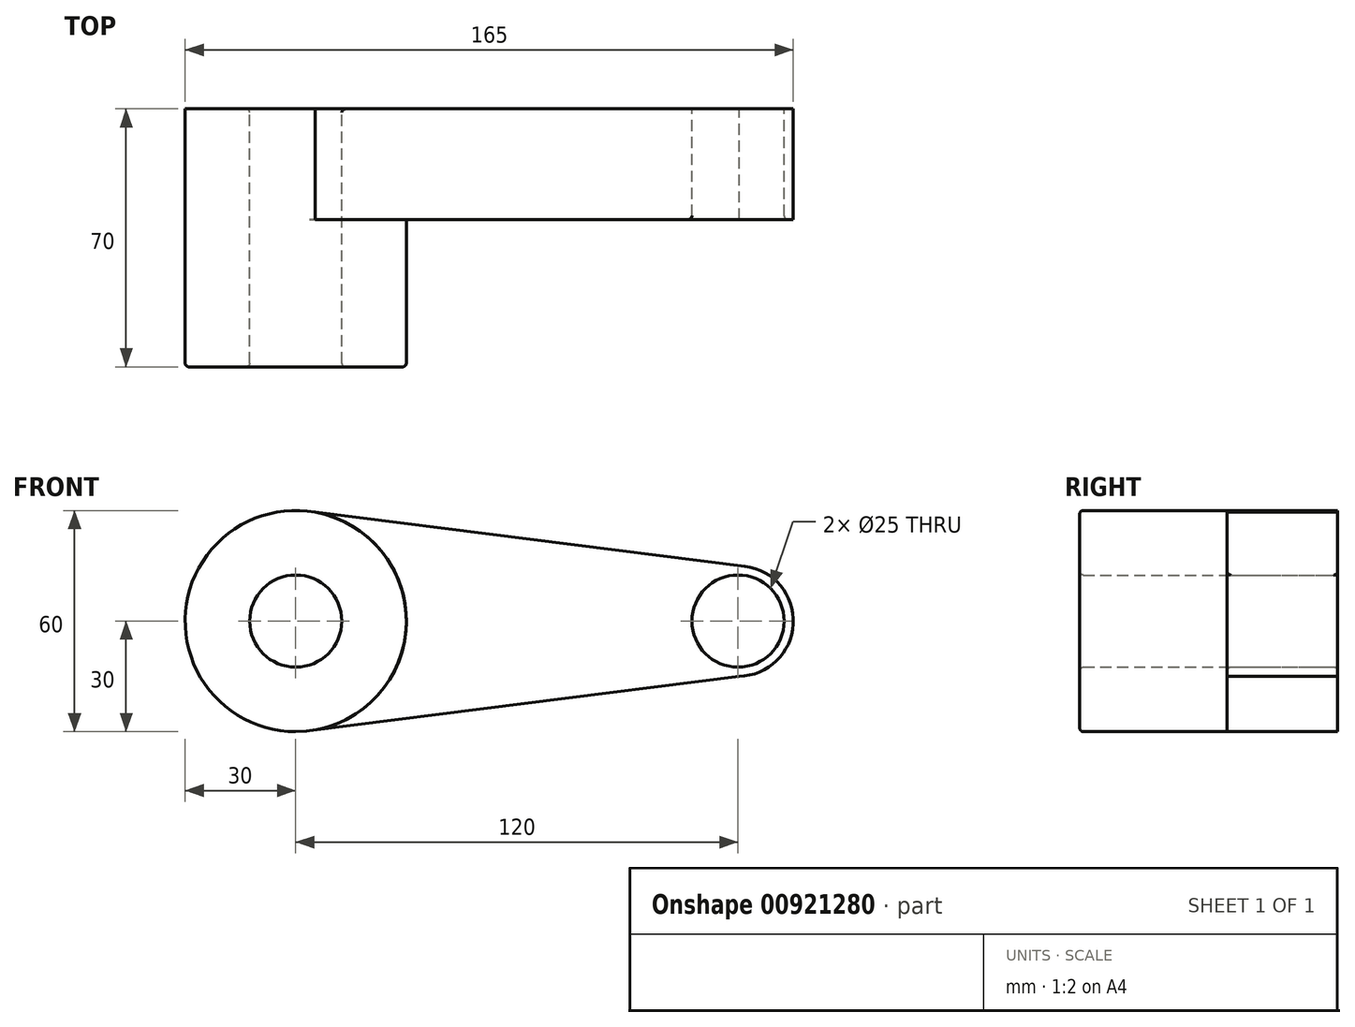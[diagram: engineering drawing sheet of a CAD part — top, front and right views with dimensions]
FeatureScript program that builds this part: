
annotation { "Feature Type Name" : "Feature", "Feature Type Description" : "" }
export const myFeature = defineFeature(function(context is Context, id is Id, definition is map)
    precondition{}
    {
        {
            var Q0;
            Q0=qCreatedBy(makeId("Front.planeOp"),FACE);
            var sketch = newSketch(context, id + "F0", { "sketchPlane" : qUnion([Q0])});
            skCircle(sketch, "E0", {"center": v(0, 0) * mm, "radius": 30 * mm});
            skCircle(sketch, "E1", {"center": v(120, 0) * mm, "radius": 15 * mm});
            skLineSegment(sketch, "E2", {"start": v(120.3, -15) * mm, "end": v(3.77, -29.76) * mm});
            skLineSegment(sketch, "E3", {"start": v(5.2, 29.54) * mm, "end": v(121.87, 14.88) * mm});
            skCircle(sketch, "E4", {"center": v(0, 0) * mm, "radius": 12.5 * mm});
            skCircle(sketch, "E5", {"center": v(120, 0) * mm, "radius": 12.5 * mm});
            skSolve(sketch);
        }
        {
            var Q0;
            Q0 = qSketchRegion(id + "F0", true);
            extrude(context, id + "F1", {"entities" : qUnion([Q0]), "depth" : 30 * mm, "offsetDistance" : 25.4 * mm});
        }
        {
            var Q0;
            Q0=makeQuery(id+"F0.imprint","IMPRINT",FACE,{"disambiguationData":[TD([[makeQuery(id+"F0.imprint","IMPRINT",EDGE,{"derivedFrom":sQuery(id+"F0.wireOp",EDGE,"E4")}),-1.0]])]});
            extrude(context, id + "F2", {"entities" : qUnion([Q0]), "operationType" : NewBodyOperationType.ADD, "depth" : 70 * mm, "offsetDistance" : 25.4 * mm});
        }
        {
            var Q0;
            Q0=makeQuery(id+"F2.opExtrude","CAP_EDGE",EDGE,{"disambiguationData":[OSD([sQuery(id+"F0.wireOp",EDGE,"E0")])],"isStart":false});
            var Q1;
            Q1=makeQuery(id+"F2.opExtrude","CAP_EDGE",EDGE,{"disambiguationData":[OSD([sQuery(id+"F0.wireOp",EDGE,"E4")])],"isStart":false});
            var Q2;
            Q2=makeQuery(id+"F1.opExtrude","CAP_EDGE",EDGE,{"disambiguationData":[OSD([sQuery(id+"F0.wireOp",EDGE,"E5")])],"isStart":false});
            fillet(context, id + "F3", {"entities" : qUnion([Q0, Q1, Q2]), "radius" : 1 * mm, "tangentPropagation" : true, "allowEdgeOverflow" : false});
        }
        {
            var Q0;
            Q0=makeQuery(id+"F1.opExtrude","CAP_EDGE",EDGE,{"disambiguationData":[OSD([sQuery(id+"F0.wireOp",EDGE,"E4")])],"isStart":true});
            fillet(context, id + "F4", {"entities" : qUnion([Q0]), "radius" : 1 * mm, "tangentPropagation" : true, "allowEdgeOverflow" : false});
        }
        {
            var Q0;
            Q0=makeQuery(id+"F1.opExtrude","CAP_EDGE",EDGE,{"disambiguationData":[OSD([sQuery(id+"F0.wireOp",EDGE,"E5")])],"isStart":true});
            fillet(context, id + "F5", {"entities" : qUnion([Q0]), "radius" : 0.5 * mm, "tangentPropagation" : true, "allowEdgeOverflow" : false});
        }
    });
